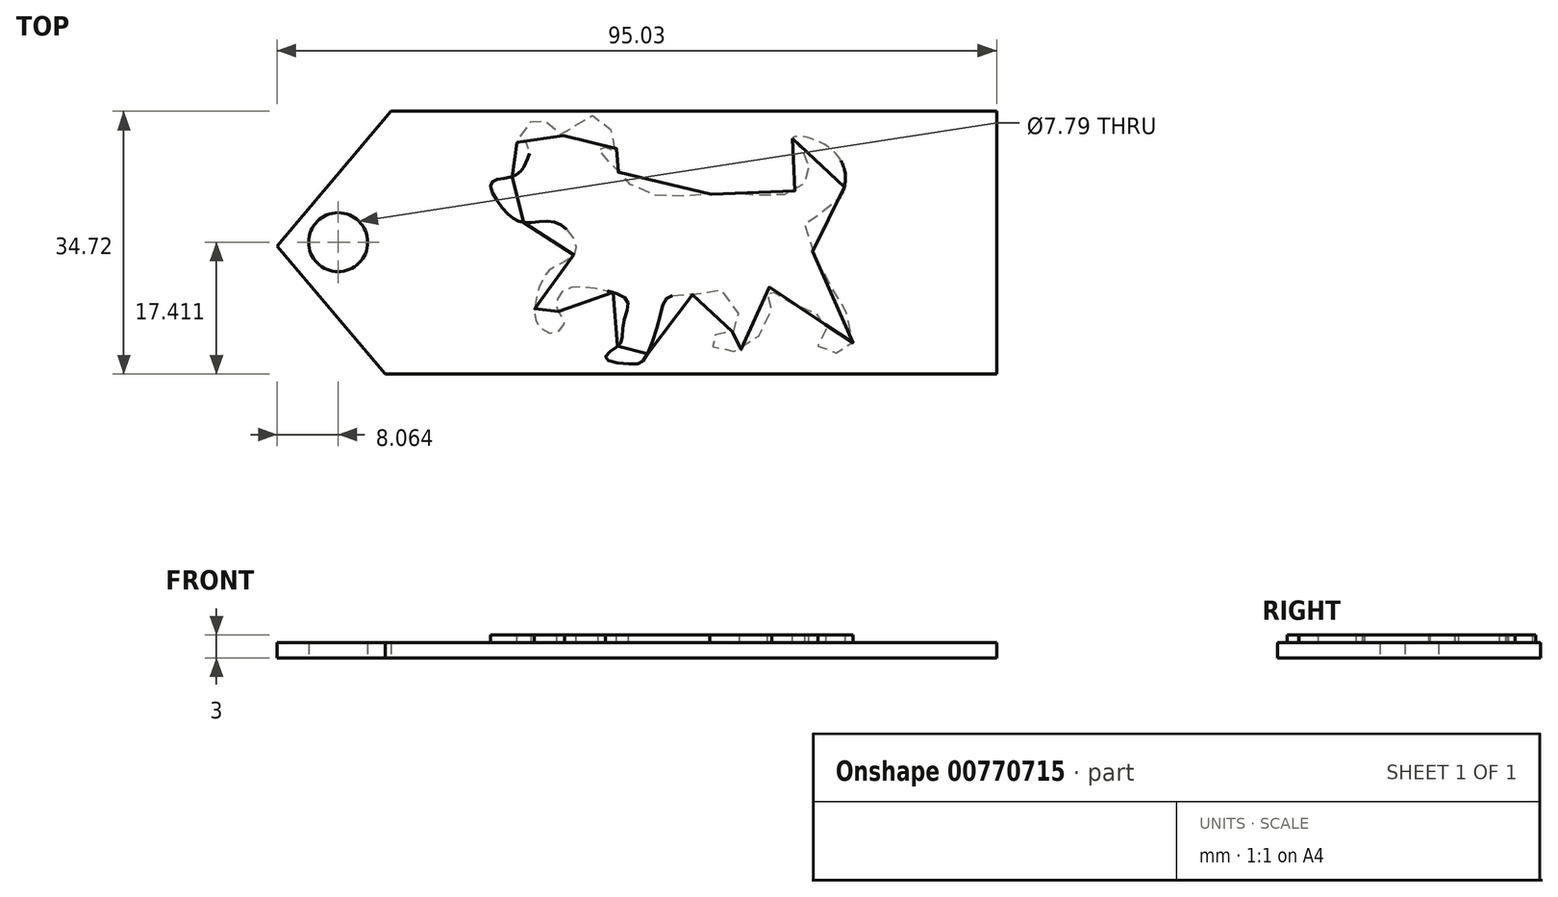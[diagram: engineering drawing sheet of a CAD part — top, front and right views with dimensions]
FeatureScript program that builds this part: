
annotation { "Feature Type Name" : "Feature", "Feature Type Description" : "" }
export const myFeature = defineFeature(function(context is Context, id is Id, definition is map)
    precondition{}
    {
        {
            var Q0;
            Q0=qCreatedBy(makeId("Top.planeOp"),FACE);
            var sketch = newSketch(context, id + "F0", { "sketchPlane" : qUnion([Q0])});
            skLineSegment(sketch, "E0", {"start": v(-61.31, -6.78) * mm, "end": v(19.42, -6.78) * mm});
            skLineSegment(sketch, "E1", {"start": v(19.42, -6.78) * mm, "end": v(19.42, 27.94) * mm});
            skLineSegment(sketch, "E2", {"start": v(19.42, 27.94) * mm, "end": v(-60.58, 27.94) * mm});
            skLineSegment(sketch, "E3", {"start": v(-60.58, 27.94) * mm, "end": v(-75.61, 10.08) * mm});
            skLineSegment(sketch, "E4", {"start": v(-75.61, 10.08) * mm, "end": v(-61.31, -6.78) * mm});
            skCircle(sketch, "E5", {"center": v(-67.55, 10.63) * mm, "radius": 3.9 * mm});
            skSolve(sketch);
        }
        {
            var Q0;
            Q0=makeQuery(id+"F0.imprint","IMPRINT",FACE,{"disambiguationData":[TD([[makeQuery(id+"F0.imprint","IMPRINT",EDGE,{"derivedFrom":sQuery(id+"F0.wireOp",EDGE,"E0")}),1.0]])]});
            extrude(context, id + "F1", {"entities" : qUnion([Q0]), "depth" : 2 * mm, "offsetDistance" : 25 * mm});
        }
        {
            var Q0;
            Q0=qCreatedBy(makeId("Top.planeOp"),FACE);
            var sketch = newSketch(context, id + "F2", { "sketchPlane" : qUnion([Q0])});
            skFitSpline(sketch, "E6", {"points": [v(-7.52, 24.35) * mm, v(-6.38, 22.93) * mm, v(-5.43, 20.84) * mm, v(-5.72, 18.75) * mm, v(-8.85, 16.85) * mm, v(-14.07, 17.04) * mm, v(-16.83, 17.13) * mm, v(-22.72, 16.66) * mm, v(-28.42, 17.9) * mm, v(-31.93, 21.5) * mm, v(-33.17, 23.12) * mm, v(-32.6, 23.4) * mm, v(-31.84, 22.74) * mm, v(-30.89, 22.74) * mm, v(-32.12, 26.35) * mm, v(-35.26, 27.01) * mm, v(-37.63, 24.73) * mm, v(-39.25, 25.87) * mm, v(-41.34, 26.92) * mm, v(-43.33, 25.02) * mm, v(-43.8, 23.69) * mm, v(-42.2, 23.69) * mm, v(-42.38, 22.07) * mm, v(-43.05, 20.55) * mm, v(-44.76, 19.22) * mm, v(-47.32, 18.46) * mm, v(-45.52, 14.76) * mm, v(-42.86, 13.24) * mm, v(-38.77, 13.24) * mm, v(-36.4, 10.96) * mm, v(-36.3, 9.15) * mm, v(-38.49, 7.63) * mm, v(-40.3, 6.2) * mm, v(-41.43, 2.88) * mm, v(-41.34, 0) * mm, v(-39.25, -1.4) * mm, v(-37.63, 0) * mm, v(-38.49, 1.55) * mm, v(-38.1, 3.93) * mm, v(-35.64, 4.78) * mm, v(-31.55, 4.12) * mm, v(-29.27, 2.79) * mm, v(-29.84, 0) * mm, v(-30.13, -2.44) * mm, v(-31.27, -3.58) * mm, v(-32.22, -4.72) * mm, v(-28.8, -5.48) * mm, v(-27.09, -4.81) * mm, v(-25, 1.08) * mm, v(-23.86, 3.45) * mm, v(-20.53, 3.74) * mm, v(-16.83, 4.3) * mm, v(-14.55, 0) * mm, v(-15.6, -1.2) * mm, v(-17.68, -1.58) * mm, v(-18.44, -2.63) * mm, v(-17.11, -3.58) * mm, v(-13.4, -3.1) * mm, v(-10.28, 1.65) * mm, v(-10.75, 2.98) * mm, v(-10.66, 4.69) * mm, v(-9.7, 3.74) * mm, v(-6.2, 2.03) * mm, v(-3.91, 0.8) * mm, v(-3.15, -1.3) * mm, v(-4.2, -3.1) * mm, v(-2.01, -3.96) * mm, v(0.37, -2.91) * mm, v(-1.06, 2.7) * mm, v(-3.44, 6.4) * mm, v(-5.81, 13.62) * mm, v(-4, 14.28) * mm, v(-0.87, 17.42) * mm, v(-1.44, 21.88) * mm, v(-5.9, 24.54) * mm, v(-7.52, 24.35) * mm]});
            skSolve(sketch);
        }
        {
            var Q0;
            Q0 = qSketchRegion(id + "F2", true);
            extrude(context, id + "F3", {"entities" : qUnion([Q0]), "operationType" : NewBodyOperationType.ADD, "depth" : 3 * mm, "offsetDistance" : 25 * mm});
        }
    });
